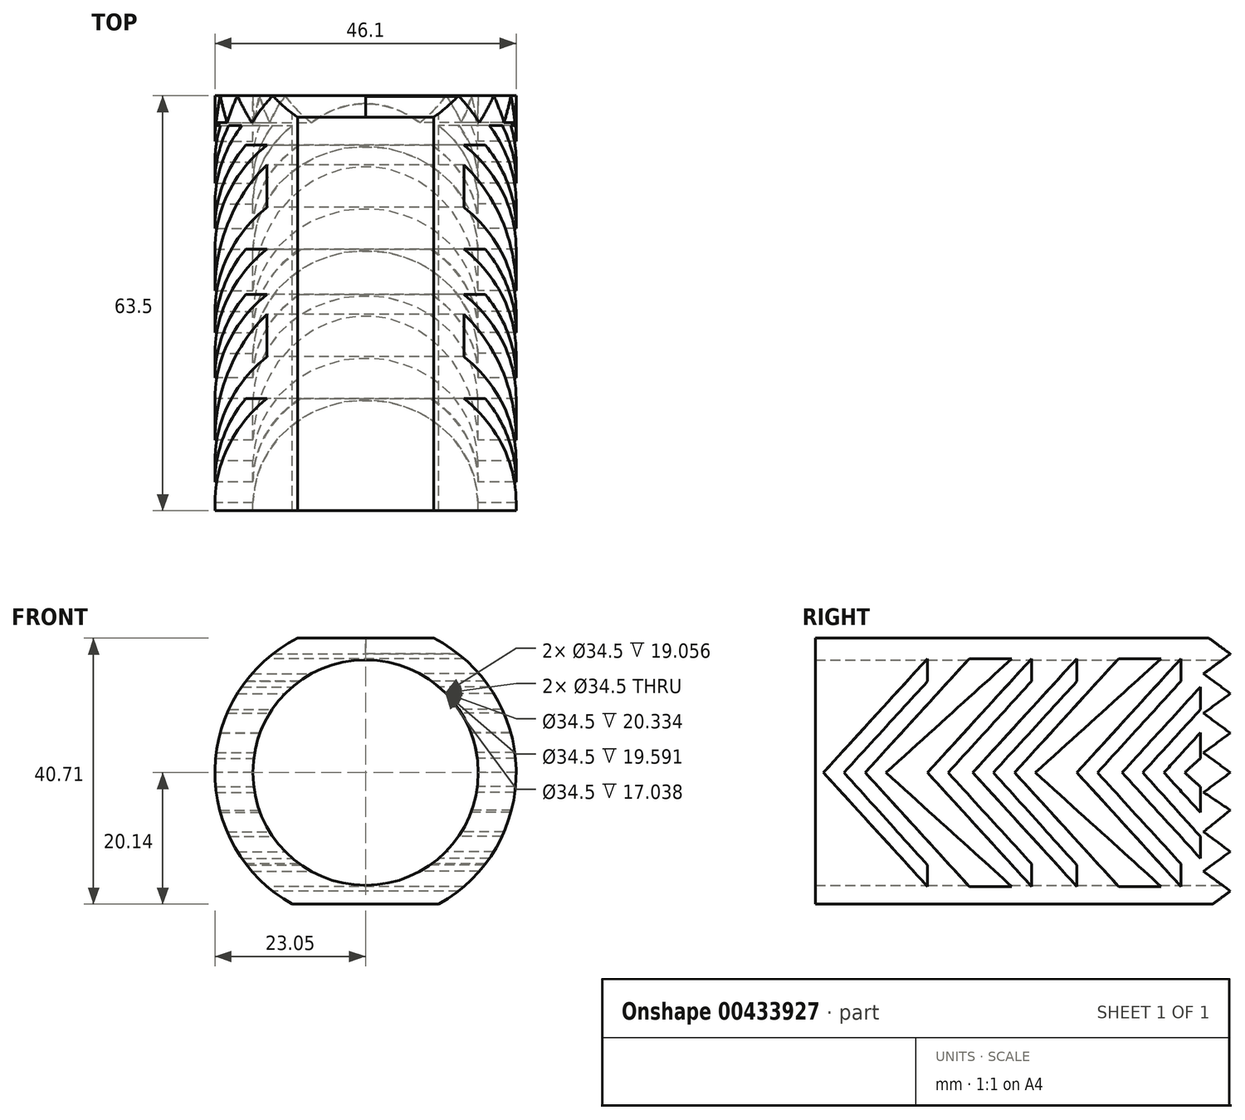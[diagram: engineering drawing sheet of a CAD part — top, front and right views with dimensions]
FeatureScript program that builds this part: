
annotation { "Feature Type Name" : "Feature", "Feature Type Description" : "" }
export const myFeature = defineFeature(function(context is Context, id is Id, definition is map)
    precondition{}
    {
        {
            var Q0;
            Q0=qCreatedBy(makeId("Front.planeOp"),FACE);
            var sketch = newSketch(context, id + "F0", { "sketchPlane" : qUnion([Q0])});
            skCircle(sketch, "E0", {"center": v(0, 0) * mm, "radius": 23.05 * mm});
            skSolve(sketch);
        }
        {
            var Q0;
            Q0 = qSketchRegion(id + "F0", true);
            extrude(context, id + "F1", {"entities" : qUnion([Q0]), "depth" : 63.5 * mm});
        }
        {
            var Q0;
            Q0=qCreatedBy(makeId("Right.planeOp"),FACE);
            var sketch = newSketch(context, id + "F2", { "sketchPlane" : qUnion([Q0])});
            skLineSegment(sketch, "E1", {"start": v(-46.35, 17.43) * mm, "end": v(-62.28, 0) * mm});
            skLineSegment(sketch, "E2", {"start": v(-62.28, 0) * mm, "end": v(-46.35, -17.44) * mm});
            skLineSegment(sketch, "E3", {"start": v(-46.35, 13.97) * mm, "end": v(-59.12, 0) * mm});
            skLineSegment(sketch, "E4", {"start": v(-59.12, 0) * mm, "end": v(-46.35, -14.17) * mm});
            skLineSegment(sketch, "E5", {"start": v(-46.35, -17.44) * mm, "end": v(-46.35, -14.17) * mm});
            skLineSegment(sketch, "E6", {"start": v(-46.35, 17.43) * mm, "end": v(-46.35, 13.97) * mm});
            skLineSegment(sketch, "E7", {"start": v(-46.35, 0) * mm, "end": v(-30.42, 17.43) * mm});
            skLineSegment(sketch, "E8", {"start": v(-30.42, 17.43) * mm, "end": v(-46.35, 0) * mm});
            skLineSegment(sketch, "E9", {"start": v(-46.35, 0) * mm, "end": v(-30.42, -17.44) * mm});
            skLineSegment(sketch, "E10", {"start": v(-30.42, 17.43) * mm, "end": v(-30.42, 13.98) * mm});
            skLineSegment(sketch, "E11", {"start": v(-30.42, -17.44) * mm, "end": v(-30.42, -13.99) * mm});
            skLineSegment(sketch, "E12", {"start": v(-30.42, -13.99) * mm, "end": v(-43.2, 0) * mm});
            skLineSegment(sketch, "E13", {"start": v(-43.2, 0) * mm, "end": v(-30.42, 13.98) * mm});
            skLineSegment(sketch, "E14", {"start": v(-52.74, 0) * mm, "end": v(-52.7, 0) * mm});
            skLineSegment(sketch, "E15", {"start": v(-55.88, 0) * mm, "end": v(-39.95, 17.43) * mm});
            skLineSegment(sketch, "E16", {"start": v(-52.7, 0) * mm, "end": v(-33.43, 17.43) * mm});
            skPoint(sketch, "E17.end.orphan", {"position": v(-36.8, 17.43) * mm});
            skPoint(sketch, "E17.start.orphan", {"position": v(-52.74, 0) * mm});
            skLineSegment(sketch, "E18.MirrorCS", {"start": v(-52.7, 0) * mm, "end": v(-33.43, -17.43) * mm});
            skLineSegment(sketch, "E19.MirrorCS", {"start": v(-55.88, 0) * mm, "end": v(-39.95, -17.43) * mm});
            skLineSegment(sketch, "E20.MirrorCS", {"start": v(-33.43, -17.43) * mm, "end": v(-39.95, -17.43) * mm});
            skLineSegment(sketch, "E21", {"start": v(-39.95, 17.43) * mm, "end": v(-33.43, 17.43) * mm});
            skLineSegment(sketch, "E22", {"start": v(-39.95, -17.43) * mm, "end": v(-33.43, -17.43) * mm});
            skLineSegment(sketch, "E23.1.0.0", {"start": v(-7.56, 17.43) * mm, "end": v(-23.49, 0) * mm});
            skLineSegment(sketch, "E23.1.0.1", {"start": v(-20.33, 0) * mm, "end": v(-7.56, 13.98) * mm});
            skLineSegment(sketch, "E23.1.0.2", {"start": v(-7.56, -13.99) * mm, "end": v(-20.33, 0) * mm});
            skLineSegment(sketch, "E23.1.0.3", {"start": v(-23.49, 0) * mm, "end": v(-7.56, -17.44) * mm});
            skLineSegment(sketch, "E23.1.0.4", {"start": v(-7.56, -17.44) * mm, "end": v(-7.56, -13.99) * mm});
            skLineSegment(sketch, "E23.1.0.5", {"start": v(-7.56, 17.43) * mm, "end": v(-7.56, 13.98) * mm});
            skLineSegment(sketch, "E23.1.0.6", {"start": v(-29.85, 0) * mm, "end": v(-10.57, 17.43) * mm});
            skLineSegment(sketch, "E23.1.0.7", {"start": v(-33.02, 0) * mm, "end": v(-17.1, 17.43) * mm});
            skLineSegment(sketch, "E23.1.0.8", {"start": v(-17.1, 17.43) * mm, "end": v(-10.57, 17.43) * mm});
            skLineSegment(sketch, "E23.1.0.9", {"start": v(-29.85, 0) * mm, "end": v(-10.57, -17.43) * mm});
            skLineSegment(sketch, "E23.1.0.10", {"start": v(-33.02, 0) * mm, "end": v(-17.1, -17.43) * mm});
            skLineSegment(sketch, "E23.1.0.11", {"start": v(-10.57, -17.43) * mm, "end": v(-17.1, -17.43) * mm});
            skLineSegment(sketch, "E23.1.0.12", {"start": v(-39.42, 0) * mm, "end": v(-23.49, -17.44) * mm});
            skLineSegment(sketch, "E23.1.0.13", {"start": v(-36.26, 0) * mm, "end": v(-23.49, -14.17) * mm});
            skLineSegment(sketch, "E23.1.0.14", {"start": v(-23.49, -17.44) * mm, "end": v(-23.49, -14.17) * mm});
            skLineSegment(sketch, "E23.1.0.15", {"start": v(-23.49, 13.97) * mm, "end": v(-36.26, 0) * mm});
            skLineSegment(sketch, "E23.1.0.16", {"start": v(-23.49, 17.43) * mm, "end": v(-39.42, 0) * mm});
            skLineSegment(sketch, "E23.1.0.17", {"start": v(-23.49, 17.43) * mm, "end": v(-23.49, 13.97) * mm});
            skLineSegment(sketch, "E23.2.0.6", {"start": v(-6.99, 0) * mm, "end": v(-4.59, 2.17) * mm});
            skLineSegment(sketch, "E23.2.0.7", {"start": v(-10.16, 0) * mm, "end": v(-4.59, 6.1) * mm});
            skLineSegment(sketch, "E23.2.0.9", {"start": v(-6.99, 0) * mm, "end": v(-4.59, -2.17) * mm});
            skLineSegment(sketch, "E23.2.0.12", {"start": v(-16.56, 0) * mm, "end": v(-4.59, -13.1) * mm});
            skLineSegment(sketch, "E23.2.0.13", {"start": v(-13.4, 0) * mm, "end": v(-4.59, -9.78) * mm});
            skLineSegment(sketch, "E23.2.0.15", {"start": v(-4.59, 9.64) * mm, "end": v(-13.4, 0) * mm});
            skLineSegment(sketch, "E23.2.0.16", {"start": v(-4.59, 13.1) * mm, "end": v(-16.56, 0) * mm});
            skLineSegment(sketch, "E23.direction1", {"start": v(-46.35, 0) * mm, "end": v(-23.49, 0) * mm, "construction": true});
            skPoint(sketch, "E24.orphan", {"position": v(12.29, -17.43) * mm});
            skPoint(sketch, "E25.orphan", {"position": v(5.77, -17.43) * mm});
            skLineSegment(sketch, "E26", {"start": v(-4.59, -6.1) * mm, "end": v(-10.16, 0) * mm});
            skLineSegment(sketch, "E27", {"start": v(-4.59, 6.1) * mm, "end": v(-4.59, 2.17) * mm});
            skLineSegment(sketch, "E28", {"start": v(-4.59, -2.17) * mm, "end": v(-4.59, -6.1) * mm});
            skLineSegment(sketch, "E29", {"start": v(-4.59, -9.78) * mm, "end": v(-4.59, -13.1) * mm});
            skLineSegment(sketch, "E30", {"start": v(-4.59, 9.64) * mm, "end": v(-4.59, 13.1) * mm});
            skPoint(sketch, "E31.end.orphan", {"position": v(-0.63, 5.75) * mm});
            skPoint(sketch, "E31.start.orphan", {"position": v(0.42, 11.58) * mm});
            skPoint(sketch, "E23.2.0.17.end.orphan", {"position": v(0.42, 15.12) * mm});
            skPoint(sketch, "E32.orphan", {"position": v(-0.63, -5.75) * mm});
            skLineSegment(sketch, "E33", {"start": v(0, 0) * mm, "end": v(-4.1, 3.03) * mm});
            skLineSegment(sketch, "E34", {"start": v(0, 0) * mm, "end": v(-4.1, -3.02) * mm});
            skLineSegment(sketch, "E35", {"start": v(-4.1, 9.08) * mm, "end": v(-0.01, 6.05) * mm});
            skPoint(sketch, "E35.endSnap0", {"position": v(-4.1, 6.05) * mm});
            skLineSegment(sketch, "E36", {"start": v(-0.01, 6.05) * mm, "end": v(-4.1, 3.03) * mm});
            skLineSegment(sketch, "E37", {"start": v(-4.1, 15.12) * mm, "end": v(0, 12.1) * mm});
            skPoint(sketch, "E37.endSnap0", {"position": v(-4.1, 12.1) * mm});
            skLineSegment(sketch, "E38", {"start": v(0, 12.1) * mm, "end": v(-4.1, 9.08) * mm});
            skLineSegment(sketch, "E39", {"start": v(-4.1, 21.17) * mm, "end": v(0, 18.14) * mm});
            skPoint(sketch, "E39.endSnap0", {"position": v(-4.1, 18.14) * mm});
            skLineSegment(sketch, "E40", {"start": v(0, 18.14) * mm, "end": v(-4.1, 15.12) * mm});
            skLineSegment(sketch, "E41", {"start": v(-4.1, -3.02) * mm, "end": v(0, -5.75) * mm});
            skLineSegment(sketch, "E42", {"start": v(0, -5.75) * mm, "end": v(-4.1, -9.07) * mm});
            skLineSegment(sketch, "E43", {"start": v(-4.1, -9.07) * mm, "end": v(0, -12.09) * mm});
            skPoint(sketch, "E43.endSnap0", {"position": v(-4.1, -12.09) * mm});
            skLineSegment(sketch, "E44", {"start": v(0, -12.09) * mm, "end": v(-4.1, -15.11) * mm});
            skPoint(sketch, "E45.endSnap0", {"position": v(-4.1, -18.13) * mm});
            skLineSegment(sketch, "E46", {"start": v(-4.1, 21.17) * mm, "end": v(0, 21.17) * mm});
            skLineSegment(sketch, "E47", {"start": v(-4.1, -21.16) * mm, "end": v(0, -21.16) * mm});
            skPoint(sketch, "E45.end.orphan", {"position": v(0.95, -18.13) * mm});
            skLineSegment(sketch, "E48", {"start": v(-4.1, -15.11) * mm, "end": v(0, -18.13) * mm});
            skLineSegment(sketch, "E49", {"start": v(0, -18.13) * mm, "end": v(-4.1, -21.16) * mm});
            skLineSegment(sketch, "E50", {"start": v(0, -21.16) * mm, "end": v(0, 21.17) * mm});
            skSolve(sketch);
        }
        {
            var Q0;
            Q0 = qSketchRegion(id + "F2", true);
            extrude(context, id + "F3", {"entities" : qUnion([Q0]), "operationType" : NewBodyOperationType.REMOVE, "depth" : 254 * mm});
        }
        {
            var Q0;
            Q0=makeQuery(id+"F3.boolean.opBoolean","COPY",FACE,{"derivedFrom":makeQuery(id+"F3.opExtrude","CAP_FACE",FACE,{"disambiguationData":[OSD([sQuery(id+"F2.wireOp",EDGE,"E15"),sQuery(id+"F2.wireOp",EDGE,"E16"),sQuery(id+"F2.wireOp",EDGE,"E18.MirrorCS"),sQuery(id+"F2.wireOp",EDGE,"E19.MirrorCS"),sQuery(id+"F2.wireOp",EDGE,"E21"),sQuery(id+"F2.wireOp",EDGE,"E22")])],"isStart":true})});
            var sketch = newSketch(context, id + "F4", { "sketchPlane" : qUnion([Q0])});
            skSolve(sketch);
        }
        {
            var Q0;
            Q0=makeQuery(id+"F4.imprint","IMPRINT",FACE,{"disambiguationData":[TD([[makeQuery(id+"F4.imprint","IMPRINT",EDGE,{"derivedFrom":makeQuery(id+"F3.boolean.opBoolean","COPY",EDGE,{"derivedFrom":makeQuery(id+"F3.opExtrude","CAP_EDGE",EDGE,{"disambiguationData":[OSD([sQuery(id+"F2.wireOp",EDGE,"E15")])],"isStart":true})})}),-1.0]])]});
            extrude(context, id + "F5", {"entities" : qUnion([Q0]), "operationType" : NewBodyOperationType.REMOVE, "oppositeDirection" : true, "depth" : 254 * mm});
        }
        {
            var Q0;
            Q0=makeQuery(id+"F3.boolean.opBoolean","COPY",FACE,{"derivedFrom":makeQuery(id+"F3.opExtrude","CAP_FACE",FACE,{"disambiguationData":[OSD([sQuery(id+"F2.wireOp",EDGE,"E1"),sQuery(id+"F2.wireOp",EDGE,"E2"),sQuery(id+"F2.wireOp",EDGE,"E3"),sQuery(id+"F2.wireOp",EDGE,"E4"),sQuery(id+"F2.wireOp",EDGE,"E5"),sQuery(id+"F2.wireOp",EDGE,"E6")])],"isStart":true})});
            extrude(context, id + "F6", {"entities" : qUnion([Q0]), "operationType" : NewBodyOperationType.REMOVE, "oppositeDirection" : true, "depth" : 254 * mm});
        }
        {
            var Q0;
            Q0=makeQuery(id+"F3.boolean.opBoolean","COPY",FACE,{"derivedFrom":makeQuery(id+"F3.opExtrude","CAP_FACE",FACE,{"disambiguationData":[OSD([sQuery(id+"F2.wireOp",EDGE,"E8"),sQuery(id+"F2.wireOp",EDGE,"E9"),sQuery(id+"F2.wireOp",EDGE,"E10"),sQuery(id+"F2.wireOp",EDGE,"E11"),sQuery(id+"F2.wireOp",EDGE,"E12"),sQuery(id+"F2.wireOp",EDGE,"E13")])],"isStart":true})});
            extrude(context, id + "F7", {"entities" : qUnion([Q0]), "operationType" : NewBodyOperationType.REMOVE, "oppositeDirection" : true, "depth" : 254 * mm});
        }
        {
            var Q0;
            Q0=qCreatedBy(makeId("Front.planeOp"),FACE);
            var sketch = newSketch(context, id + "F8", { "sketchPlane" : qUnion([Q0])});
            skCircle(sketch, "E51", {"center": v(0, 0) * mm, "radius": 17.25 * mm});
            skSolve(sketch);
        }
        {
            var Q0;
            Q0 = qSketchRegion(id + "F8", true);
            extrude(context, id + "F9", {"entities" : qUnion([Q0]), "operationType" : NewBodyOperationType.REMOVE, "depth" : 254 * mm});
        }
        {
            var Q0;
            Q0 = qSketchRegion(id + "F2", true);
            extrude(context, id + "F10", {"entities" : qUnion([Q0]), "operationType" : NewBodyOperationType.REMOVE, "oppositeDirection" : true, "depth" : 5080 * mm});
        }
        {
            var Q0;
            Q0 = qSketchRegion(id + "F2", true);
            extrude(context, id + "F11", {"entities" : qUnion([Q0]), "operationType" : NewBodyOperationType.REMOVE, "depth" : 5080 * mm});
        }
        {
            var Q0;
            Q0=qCreatedBy(makeId("Right.planeOp"),FACE);
            var sketch = newSketch(context, id + "F12", { "sketchPlane" : qUnion([Q0])});
            skLineSegment(sketch, "E52", {"start": v(0, 18.14) * mm, "end": v(-8.5, 24.55) * mm});
            skLineSegment(sketch, "E53", {"start": v(-8.5, 24.55) * mm, "end": v(3.36, 25.43) * mm});
            skLineSegment(sketch, "E54", {"start": v(3.36, 25.43) * mm, "end": v(0, 18.14) * mm});
            skSolve(sketch);
        }
        {
            var Q0;
            Q0 = qSketchRegion(id + "F12", true);
            extrude(context, id + "F13", {"entities" : qUnion([Q0]), "operationType" : NewBodyOperationType.REMOVE, "depth" : 5080 * mm});
        }
        {
            var Q0;
            Q0=qCreatedBy(makeId("Right.planeOp"),FACE);
            var sketch = newSketch(context, id + "F14", { "sketchPlane" : qUnion([Q0])});
            skLineSegment(sketch, "E55", {"start": v(0, 18.14) * mm, "end": v(-7.88, 23.94) * mm});
            skLineSegment(sketch, "E56", {"start": v(-7.88, 23.94) * mm, "end": v(0.72, 23.94) * mm});
            skLineSegment(sketch, "E57", {"start": v(0.72, 23.94) * mm, "end": v(0, 18.14) * mm});
            skSolve(sketch);
        }
        {
            var Q0;
            Q0 = qSketchRegion(id + "F14", true);
            extrude(context, id + "F15", {"entities" : qUnion([Q0]), "operationType" : NewBodyOperationType.REMOVE, "oppositeDirection" : true, "depth" : 5080 * mm});
        }
        {
            var Q0;
            Q0=qCreatedBy(makeId("Right.planeOp"),FACE);
            var sketch = newSketch(context, id + "F16", { "sketchPlane" : qUnion([Q0])});
            skLineSegment(sketch, "E58", {"start": v(-3.41, -20.7) * mm, "end": v(-7.92, -23.6) * mm});
            skLineSegment(sketch, "E59", {"start": v(-7.92, -23.6) * mm, "end": v(0.7, -23.6) * mm});
            skLineSegment(sketch, "E60", {"start": v(0.7, -23.6) * mm, "end": v(0.88, -19.95) * mm});
            skLineSegment(sketch, "E61", {"start": v(0.88, -19.95) * mm, "end": v(-3.41, -20.7) * mm});
            skSolve(sketch);
        }
        {
            var Q0;
            Q0 = qSketchRegion(id + "F16", true);
            extrude(context, id + "F17", {"entities" : qUnion([Q0]), "operationType" : NewBodyOperationType.REMOVE, "depth" : 5080 * mm});
        }
        {
            var Q0;
            Q0=qCreatedBy(makeId("Right.planeOp"),FACE);
            var sketch = newSketch(context, id + "F18", { "sketchPlane" : qUnion([Q0])});
            skLineSegment(sketch, "E62", {"start": v(-3.58, -20.85) * mm, "end": v(-9.4, -24.3) * mm});
            skLineSegment(sketch, "E63", {"start": v(-9.4, -24.3) * mm, "end": v(1.72, -23.9) * mm});
            skLineSegment(sketch, "E64", {"start": v(1.72, -23.9) * mm, "end": v(1.59, -20.22) * mm});
            skLineSegment(sketch, "E65", {"start": v(1.59, -20.22) * mm, "end": v(-3.58, -20.85) * mm});
            skSolve(sketch);
        }
        {
            var Q0;
            Q0 = qSketchRegion(id + "F18", true);
            extrude(context, id + "F19", {"entities" : qUnion([Q0]), "operationType" : NewBodyOperationType.REMOVE, "oppositeDirection" : true, "depth" : 5080 * mm});
        }
        {
            var Q0;
            Q0=qCreatedBy(makeId("Right.planeOp"),FACE);
            var sketch = newSketch(context, id + "F20", { "sketchPlane" : qUnion([Q0])});
            skLineSegment(sketch, "E66", {"start": v(2.37, 20.67) * mm, "end": v(-81.12, 20.67) * mm});
            skLineSegment(sketch, "E67", {"start": v(-81.12, 20.67) * mm, "end": v(-67.3, 26.44) * mm});
            skLineSegment(sketch, "E68", {"start": v(-67.3, 26.44) * mm, "end": v(-0.59, 26.44) * mm});
            skLineSegment(sketch, "E69", {"start": v(-0.59, 26.44) * mm, "end": v(2.37, 20.67) * mm});
            skSolve(sketch);
        }
        {
            var Q0;
            Q0 = qSketchRegion(id + "F20", true);
            extrude(context, id + "F21", {"entities" : qUnion([Q0]), "operationType" : NewBodyOperationType.REMOVE, "oppositeDirection" : true, "depth" : 5080 * mm});
        }
        {
            var Q0;
            Q0=qCreatedBy(makeId("Front.planeOp"),FACE);
            var sketch = newSketch(context, id + "F22", { "sketchPlane" : qUnion([Q0])});
            skLineSegment(sketch, "E70", {"start": v(-13.8, 20.57) * mm, "end": v(15.77, 20.57) * mm});
            skLineSegment(sketch, "E71", {"start": v(15.77, 20.57) * mm, "end": v(14.64, 28.82) * mm});
            skLineSegment(sketch, "E72", {"start": v(14.64, 28.82) * mm, "end": v(-12.84, 28.82) * mm});
            skLineSegment(sketch, "E73", {"start": v(-12.84, 28.82) * mm, "end": v(-13.8, 20.57) * mm});
            skSolve(sketch);
        }
        {
            var Q0;
            Q0 = qSketchRegion(id + "F22", true);
            extrude(context, id + "F23", {"entities" : qUnion([Q0]), "operationType" : NewBodyOperationType.REMOVE, "depth" : 254 * mm});
        }
        {
            var Q0;
            Q0=qCreatedBy(makeId("Front.planeOp"),FACE);
            var sketch = newSketch(context, id + "F24", { "sketchPlane" : qUnion([Q0])});
            skLineSegment(sketch, "E74", {"start": v(27.33, -20.14) * mm, "end": v(-16.41, -20.14) * mm});
            skLineSegment(sketch, "E75", {"start": v(-16.41, -20.14) * mm, "end": v(-18.59, -25.67) * mm});
            skLineSegment(sketch, "E76", {"start": v(-18.59, -25.67) * mm, "end": v(26.82, -25.67) * mm});
            skLineSegment(sketch, "E77", {"start": v(26.82, -25.67) * mm, "end": v(27.33, -20.14) * mm});
            skSolve(sketch);
        }
        {
            var Q0;
            Q0 = qSketchRegion(id + "F24", true);
            extrude(context, id + "F25", {"entities" : qUnion([Q0]), "operationType" : NewBodyOperationType.REMOVE, "depth" : 254 * mm});
        }
    });
